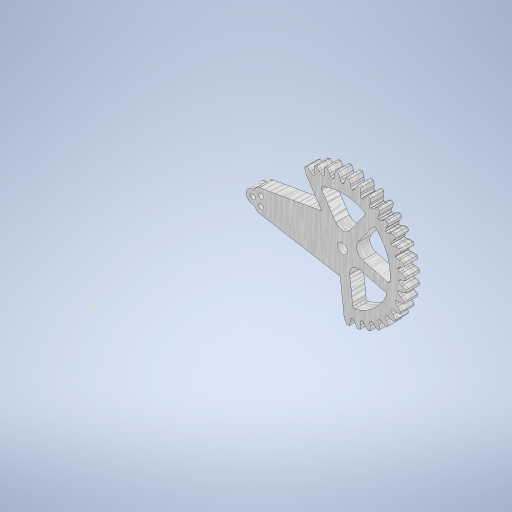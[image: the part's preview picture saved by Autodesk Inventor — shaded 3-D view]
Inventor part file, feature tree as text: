
AUTODESK INVENTOR PART (.ipt)
format: ipt  version: 2023 (Build 270158000, 158)  size: 2,695,168 bytes
history: native  units: mm
features: sketch x11, extrude x10, fillet x7, other x6, projected_geometry x3, hole x2
ambient origin geometry x8: Origin, YZ Plane, XZ Plane, XY Plane, X Axis, Y Axis, Z Axis, Center Point
bodies: Body1 (feature_tree), Body2 (feature_tree)
feature tree (39):
  other  "ソリッド1"
  extrude  "押し出し1"  Depth=8.0mm TaperAngle=0.0deg
  sketch  "スケッチ2"
  extrude  "押し出し2"  Depth=8.0mm TaperAngle=0.0deg
  hole  "穴1"  [1 undecoded]
  fillet  "フィレット1"  Radius=1.0mm
  fillet  "フィレット2"  Radius=18.0mm
  sketch  "スケッチ3"
  sketch  "スケッチ4"
  sketch  "スケッチ5"
  extrude  "押し出し3"  Depth=8.0mm TaperAngle=0.0deg
  extrude  "押し出し4"  Depth=10.0mm TaperAngle=0.0deg
  extrude  "押し出し5"  Depth=5.0mm
  extrude  "押し出し6"  Depth=10.0mm TaperAngle=0.0deg
  extrude  "押し出し7"  Depth=30.0mm
  fillet  "フィレット3"  Radius=8.0mm
  fillet  "フィレット4"  Radius=18.0mm
  fillet  "フィレット5"  Radius=6.0mm
  fillet  "フィレット6"  Radius=6.0mm
  sketch  "スケッチ9"
  extrude  "押し出し8"  Depth=6.0mm
  extrude  "押し出し9"  Depth=6.0mm
  hole  "穴2"  [1 undecoded]
  extrude  "押し出し10"  Depth=12.01385mm
  fillet  "フィレット7"  Radius=12.01385mm
  sketch  "スケッチ11"
  sketch  "スケッチ1"
  projected_geometry  "投影ループ1"
  sketch  "スケッチ6"
  sketch  "スケッチ7"
  sketch  "スケッチ8"
  sketch  "スケッチ10"
  projected_geometry  "投影ループ2"
  projected_geometry  "投影ループ3"
  other  "断面エッジを投影1"
  other  "断面エッジを投影2"
  other  "断面エッジを投影3"
  other  "断面エッジを投影4"
  other  "断面エッジを投影5"
note: 2 required parameter values undecoded (feature->parameter linkage not recoverable at this tier; creation-order binding heuristic only, values carry confidence <= 0.55)
